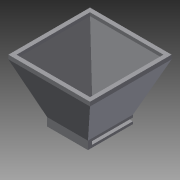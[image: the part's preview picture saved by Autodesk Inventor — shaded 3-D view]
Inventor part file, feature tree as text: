
AUTODESK INVENTOR PART (.ipt)
format: ipt  version: 2014 SP2 (Build 180246200, 246)  size: 144,384 bytes
history: native  units: mm
features: extrude x4, sketch x3, other x2, projected_geometry x2, plane x1, loft x1, shell x1
ambient origin geometry x8: Origin, YZ Plane, XZ Plane, XY Plane, X Axis, Y Axis, Z Axis, Center Point
bodies: Solid1 (feature_tree)
feature tree (14):
  extrude  "Extrusion1"  Depth=55.0mm
  plane  "Work Plane1"
  extrude  "Extrusion3"  Depth=10.0mm
  loft  "Loft1"
  shell  "Shell2"  Thickness=5.0mm
  extrude  "Extrusion4"  TaperAngle=0.0deg  [1 undecoded]
  extrude  "Extrusion5"  TaperAngle=0.0deg  [1 undecoded]
  sketch  "Sketch1"  dims[d0=50.0mm d1=55.0mm]
  sketch  "Sketch3"  dims[d2=10.0mm d3=0.0mm d8=60.0mm]
  other  "Edges1"
  other  "Edges2"
  sketch  "Sketch4"  dims[d9=100.0mm d10=100.0mm d13=5.0mm d14=0.0mm d15=0.0mm d16=90.0deg d17=0.0mm d18=90.0deg d20=5.0mm d23=5.0mm d24=0.0mm d25=5.0mm d26=0.0mm d28=4.0mm d29=3.0mm d30=5.0mm d31=75.0mm]
  projected_geometry  "Projected Loop1"
  projected_geometry  "Projected Loop2"
note: 2 required parameter values undecoded (feature->parameter linkage not recoverable at this tier; creation-order binding heuristic only, values carry confidence <= 0.55)
